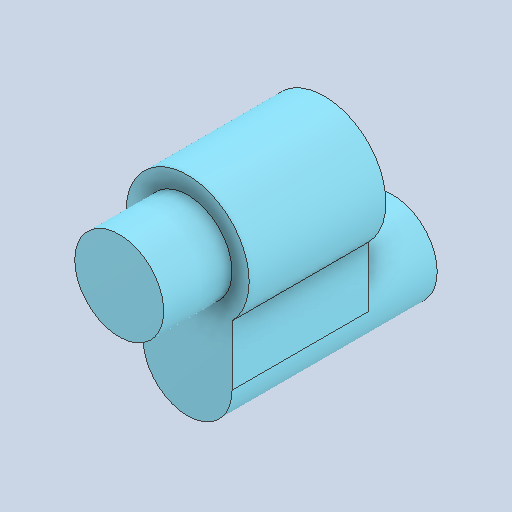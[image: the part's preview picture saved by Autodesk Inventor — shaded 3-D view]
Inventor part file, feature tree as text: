
AUTODESK INVENTOR PART (.ipt)
format: ipt  version: 2022 (Build 260153000, 153)  size: 126,976 bytes
history: native  units: in
note: dims shown in document units (in); Inventor stores cm internally (conversion verified against a paired STEP export)
features: other x3, sketch x2
ambient origin geometry x8: Origin, YZ Plane, XZ Plane, XY Plane, X Axis, Y Axis, Z Axis, Center Point
bodies: Solid1 (feature_tree)
feature tree (5):
  other  "Component29.ipt"
  other  "Solid1::Component29.ipt"
  other  "TaggingFeature1"
  sketch  "Sketch2"  dims[d0=0.3937in]
  sketch  "Sketch3"
